# Revit family: EZTE
name_source: partatom
category: Mechanical Equipment
revit_build: Autodesk Revit 2018 (Build: 20170223_1515(x64)
units: mm (PartAtom-declared; Revit-internal decimal feet)

## family parameters
Always vertical = Yes
Cut with Voids When Loaded = No
OmniClass Number = 23.75.00.00
OmniClass Title = Climate Control (HVAC)
Part Type = Normal
Room Calculation Point = No
Round Connector Dimension = Use Diameter
Shared = No
Work Plane-Based = No

## types (18) — shared parameters
Discharge = 0' - 0 5/8"
ElectricBack = 0' - 1 1/2"
Elength = 2' - 0"
EnclosureFront = 0' - 3"
EnclosureHeight = 0' - 11 3/32"
EnclosureWidth = 0' - 7 1/8"
EnslosureRear = 1' - 2 7/32"
Ewidth = 0' - 7 1/8"
Inlet_S = 0' - 5 3/8"
Length = 3' - 3 1/2"
Manufacturer = ANEMOSTAT PRODUCTS
Model = EZTE
Overlap = 0' - 0 5/8"
URL = https://www.anemostat-hvac.com

## per-type parameters (varying)
| type | Coil | Description | DischargeX | DischargeY | Eheight | EnclosureCenter | Height | HeightCenter | InletDia | InletRadius | LeftController | LeftSide Electric Enclosure | Power Left Controller | Power Right Controller | RightController | RightSide Electric Enclosure | SlipDrive | Width |
| EZTE Inlet Size 16 RH | 0' - 4 15/16" | EZTE EZTE W/ INTEGRAL ELECTRIC HEAT | 1' - 10 3/4" | 1' - 4 1/4" | 1' - 5 1/2" | 0' - 8 3/4" | 1' - 5 1/2" | 0' - 8 3/4" | 1' - 3 7/8" | 0' - 7 15/16" | No | No | No | Yes | Yes | Yes | 3' - 8 7/16" | 2' - 0" |
| EZTE Inlet Size 16 LH | 0' - 4 15/16" | EZTE EZTE W/ INTEGRAL ELECTRIC HEAT | 1' - 10 3/4" | 1' - 4 1/4" | 1' - 5 1/2" | 0' - 8 3/4" | 1' - 5 1/2" | 0' - 8 3/4" | 1' - 3 7/8" | 0' - 7 15/16" | Yes | Yes | Yes | No | No | No | 3' - 8 7/16" | 2' - 0" |
| EZTE Inlet Size 14 LH | 0' - 3 3/4" | EZTE EZTE W/ INTEGRAL ELECTRIC HEAT | 1' - 6 3/4" | 1' - 4 1/4" | 1' - 5 1/2" | 0' - 8 3/4" | 1' - 5 1/2" | 0' - 8 3/4" | 1' - 1 7/8" | 0' - 6 15/16" | Yes | Yes | Yes | No | No | No | 3' - 7 1/4" | 1' - 8" |
| EZTE Inlet Size 14 RH | 0' - 3 3/4" | EZTE EZTE W/ INTEGRAL ELECTRIC HEAT | 1' - 6 3/4" | 1' - 4 1/4" | 1' - 5 1/2" | 0' - 8 3/4" | 1' - 5 1/2" | 0' - 8 3/4" | 1' - 1 7/8" | 0' - 6 15/16" | No | No | No | Yes | Yes | Yes | 3' - 7 1/4" | 1' - 8" |
| EZTE Inlet Size 12 RH | 0' - 3 3/4" | EZTE EZTE W/ INTEGRAL ELECTRIC HEAT | 1' - 2 3/4" | 1' - 1 3/4" | 1' - 3" | 0' - 7 1/2" | 1' - 3" | 0' - 7 1/2" | 0' - 11 7/8" | 0' - 5 15/16" | No | No | No | Yes | Yes | Yes | 3' - 7 1/4" | 1' - 4" |
| EZTE Inlet Size 12 LH | 0' - 3 3/4" | EZTE EZTE W/ INTEGRAL ELECTRIC HEAT | 1' - 2 3/4" | 1' - 1 3/4" | 1' - 3" | 0' - 7 1/2" | 1' - 3" | 0' - 7 1/2" | 0' - 11 7/8" | 0' - 5 15/16" | Yes | Yes | Yes | No | No | No | 3' - 7 1/4" | 1' - 4" |
| EZTE Inlet Size 10 LH | 0' - 6 15/16" | EZTE W/ INTEGRAL ELECTRIC HEAT | 1' - 0 3/4" | 0' - 11 1/4" | 1' - 0 1/2" | 0' - 6 1/4" | 1' - 0 1/2" | 0' - 6 1/4" | 0' - 9 7/8" | 0' - 4 15/16" | Yes | Yes | Yes | No | No | No | 3' - 10 7/16" | 1' - 2" |
| EZTE Inlet Size 09 RH | 0' - 6 15/16" | EZTE W/ INTEGRAL ELECTRIC HEAT | 1' - 0 3/4" | 0' - 11 1/4" | 1' - 0 1/2" | 0' - 6 1/4" | 1' - 0 1/2" | 0' - 6 1/4" | 0' - 8 7/8" | 0' - 4 7/16" | No | No | No | Yes | Yes | Yes | 3' - 10 7/16" | 1' - 2" |
| EZTE Inlet Size 09 LH | 0' - 6 15/16" | EZTE W/ INTEGRAL ELECTRIC HEAT | 1' - 0 3/4" | 0' - 11 1/4" | 1' - 0 1/2" | 0' - 6 1/4" | 1' - 0 1/2" | 0' - 6 1/4" | 0' - 8 7/8" | 0' - 4 7/16" | Yes | Yes | Yes | No | No | No | 3' - 10 7/16" | 1' - 2" |
| EZTE Inlet Size 08 LH | 0' - 3 3/4" | EZTE W/ INTEGRAL ELECTRIC HEAT | 0' - 10 3/4" | 0' - 8 3/4" | 1' - 0" | 0' - 5" | 0' - 10" | 0' - 6" | 0' - 7 7/8" | 0' - 3 15/16" | Yes | Yes | Yes | No | No | No | 3' - 7 1/4" | 1' - 0" |
| EZTE Inlet Size 08 RH | 0' - 3 3/4" | EZTE W/ INTEGRAL ELECTRIC HEAT | 0' - 10 3/4" | 0' - 8 3/4" | 1' - 0" | 0' - 5" | 0' - 10" | 0' - 6" | 0' - 7 7/8" | 0' - 3 15/16" | No | No | No | Yes | Yes | Yes | 3' - 7 1/4" | 1' - 0" |
| EZTE Inlet Size 07 LH | 0' - 3 3/4" | EZTE W/ INTEGRAL ELECTRIC HEAT | 0' - 10 3/4" | 0' - 8 3/4" | 1' - 0" | 0' - 5" | 0' - 10" | 0' - 6" | 0' - 6 7/8" | 0' - 3 7/16" | Yes | Yes | Yes | No | No | No | 3' - 7 1/4" | 1' - 0" |
| EZTE Inlet Size 07 RH | 0' - 3 3/4" | EZTE W/ INTEGRAL ELECTRIC HEAT | 0' - 10 3/4" | 0' - 8 3/4" | 1' - 0" | 0' - 5" | 0' - 10" | 0' - 6" | 0' - 6 7/8" | 0' - 3 7/16" | No | No | No | Yes | Yes | Yes | 3' - 7 1/4" | 1' - 0" |
| EZTE Inlet Size 06 RH | 0' - 3 3/4" | EZTE W/ INTEGRAL ELECTRIC HEAT | 0' - 8 3/4" | 0' - 8 3/4" | 1' - 0" | 0' - 5" | 0' - 10" | 0' - 6" | 0' - 5 7/8" | 0' - 2 15/16" | No | No | No | Yes | Yes | Yes | 3' - 7 1/4" | 0' - 10" |
| EZTE Inlet Size 06 LH | 0' - 3 3/4" | EZTE W/ INTEGRAL ELECTRIC HEAT | 0' - 8 3/4" | 0' - 8 3/4" | 1' - 0" | 0' - 5" | 0' - 10" | 0' - 6" | 0' - 5 7/8" | 0' - 2 15/16" | Yes | Yes | Yes | No | No | No | 3' - 7 1/4" | 0' - 10" |
| EZTE Inlet Size 05 RH | 0' - 3 3/4" | EZTE W/ INTEGRAL ELECTRIC HEAT | 0' - 8 3/4" | 0' - 8 3/4" | 1' - 0" | 0' - 5" | 0' - 10" | 0' - 6" | 0' - 4 7/8" | 0' - 2 7/16" | No | No | No | Yes | Yes | Yes | 3' - 7 1/4" | 0' - 10" |
| EZTE Inlet Size 05 LH | 0' - 6 15/16" | EZTE W/ INTEGRAL ELECTRIC HEAT | 0' - 8 3/4" | 0' - 8 3/4" | 1' - 0" | 0' - 5" | 0' - 10" | 0' - 6" | 0' - 4 7/8" | 0' - 2 7/16" | Yes | Yes | Yes | No | No | No | 3' - 10 7/16" | 0' - 10" |
| EZTE Inlet Size 10 RH | 0' - 6 15/16" | EZTE W/ INTEGRAL ELECTRIC HEAT | 1' - 0 3/4" | 0' - 11 1/4" | 1' - 0 1/2" | 0' - 6 1/4" | 1' - 0 1/2" | 0' - 6 1/4" | 0' - 9 7/8" | 0' - 4 15/16" | No | No | No | Yes | Yes | Yes | 3' - 10 7/16" | 1' - 2" |

## geometry (parser evidence)
native form markers: Sweep x6
no freeform markers — native parametric forms only
